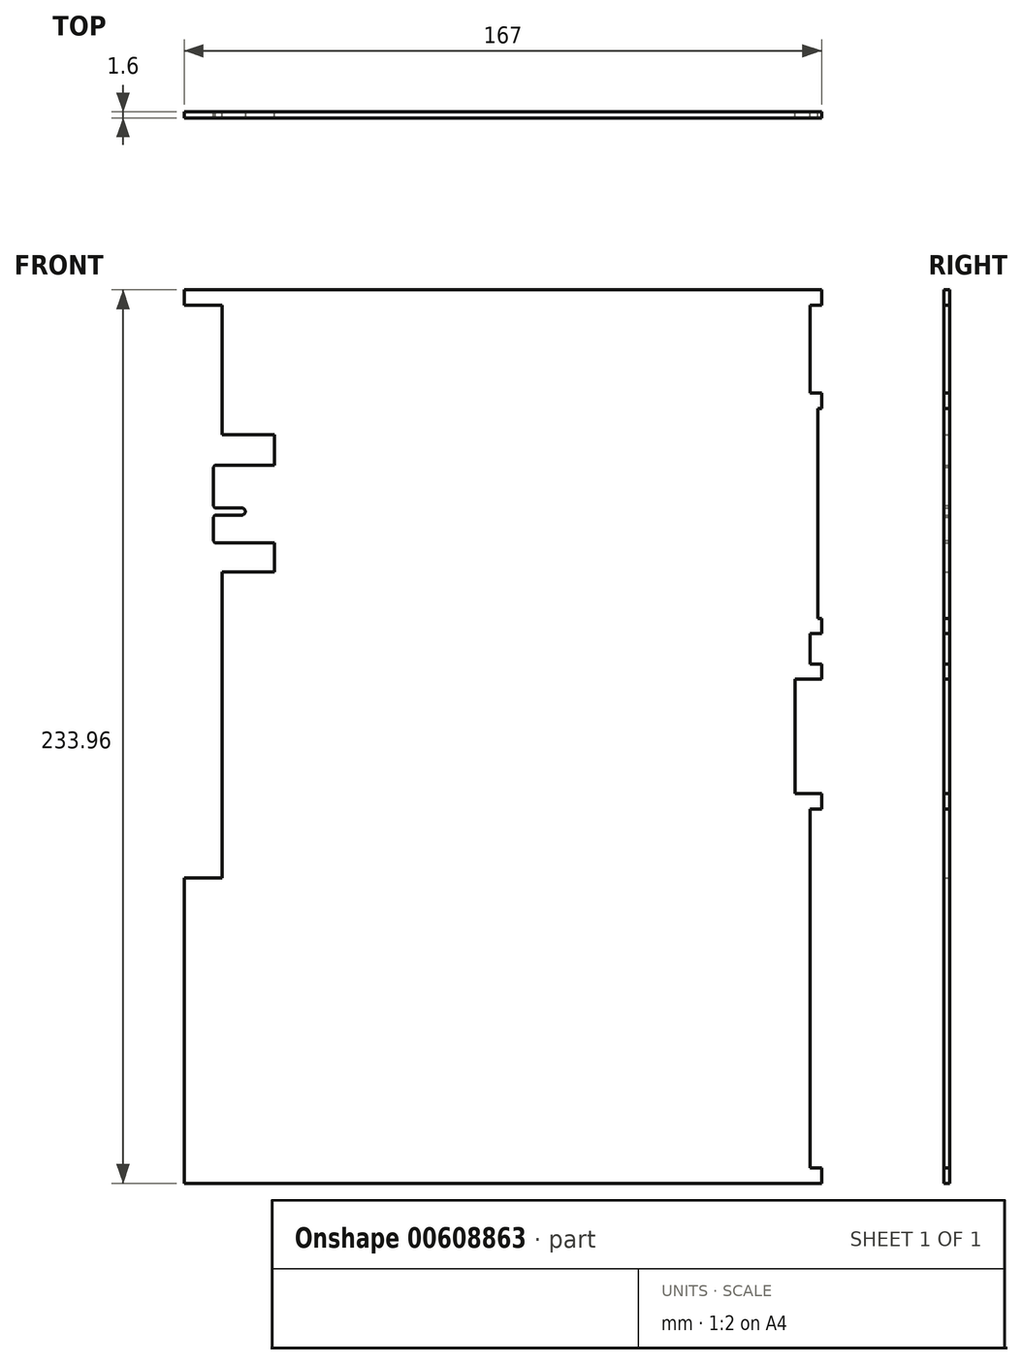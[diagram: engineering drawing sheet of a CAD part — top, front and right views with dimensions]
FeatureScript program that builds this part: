
annotation { "Feature Type Name" : "Feature", "Feature Type Description" : "" }
export const myFeature = defineFeature(function(context is Context, id is Id, definition is map)
    precondition{}
    {
        {
            var Q0;
            Q0=qCreatedBy(makeId("Front.planeOp"),FACE);
            var sketch = newSketch(context, id + "F0", { "sketchPlane" : qUnion([Q0])});
            skLineSegment(sketch, "E0.bottom", {"start": v(0, 0) * mm, "end": v(167, 0) * mm});
            skLineSegment(sketch, "E0.top", {"start": v(0, 233.96) * mm, "end": v(167, 233.96) * mm});
            skLineSegment(sketch, "E0.left", {"start": v(0, 0) * mm, "end": v(0, 233.96) * mm});
            skLineSegment(sketch, "E0.right", {"start": v(167, 0) * mm, "end": v(167, 233.96) * mm});
            skLineSegment(sketch, "E1.bottom", {"start": v(0, 229.96) * mm, "end": v(10, 229.96) * mm});
            skLineSegment(sketch, "E1.top", {"start": v(0, 79.96) * mm, "end": v(10, 79.96) * mm});
            skLineSegment(sketch, "E1.left", {"start": v(0, 229.96) * mm, "end": v(0, 79.96) * mm});
            skLineSegment(sketch, "E1.right", {"start": v(10, 229.96) * mm, "end": v(10, 79.96) * mm});
            skLineSegment(sketch, "E2.bottom", {"start": v(-12.96, 196.1) * mm, "end": v(23.6, 196.1) * mm});
            skLineSegment(sketch, "E2.top", {"start": v(-12.96, 160.1) * mm, "end": v(23.6, 160.1) * mm});
            skLineSegment(sketch, "E2.left", {"start": v(-12.96, 196.1) * mm, "end": v(-12.96, 160.1) * mm});
            skLineSegment(sketch, "E2.right", {"start": v(23.6, 196.1) * mm, "end": v(23.6, 160.1) * mm});
            skLineSegment(sketch, "E3.bottom", {"start": v(7.6, 188.07) * mm, "end": v(33.85, 188.07) * mm});
            skLineSegment(sketch, "E3.top", {"start": v(7.6, 167.77) * mm, "end": v(33.85, 167.77) * mm});
            skLineSegment(sketch, "E3.left", {"start": v(7.6, 188.07) * mm, "end": v(7.6, 167.77) * mm});
            skLineSegment(sketch, "E3.right", {"start": v(33.85, 188.07) * mm, "end": v(33.85, 167.77) * mm});
            skLineSegment(sketch, "E4.bottom", {"start": v(4.67, 176.87) * mm, "end": v(16, 176.87) * mm});
            skLineSegment(sketch, "E4.top", {"start": v(4.67, 174.97) * mm, "end": v(16, 174.97) * mm});
            skLineSegment(sketch, "E4.left", {"start": v(4.67, 176.87) * mm, "end": v(4.67, 174.97) * mm});
            skLineSegment(sketch, "E4.right", {"start": v(16, 176.87) * mm, "end": v(16, 174.97) * mm});
            skLineSegment(sketch, "E5.bottom", {"start": v(167, 4) * mm, "end": v(164, 4) * mm});
            skLineSegment(sketch, "E5.top", {"start": v(167, 98) * mm, "end": v(164, 98) * mm});
            skLineSegment(sketch, "E5.left", {"start": v(167, 4) * mm, "end": v(167, 98) * mm});
            skLineSegment(sketch, "E5.right", {"start": v(164, 4) * mm, "end": v(164, 98) * mm});
            skLineSegment(sketch, "E6.bottom", {"start": v(167, 102) * mm, "end": v(160, 102) * mm});
            skLineSegment(sketch, "E6.top", {"start": v(167, 132) * mm, "end": v(160, 132) * mm});
            skLineSegment(sketch, "E6.left", {"start": v(167, 102) * mm, "end": v(167, 132) * mm});
            skLineSegment(sketch, "E6.right", {"start": v(160, 102) * mm, "end": v(160, 132) * mm});
            skLineSegment(sketch, "E7.bottom", {"start": v(167, 136) * mm, "end": v(164, 136) * mm});
            skLineSegment(sketch, "E7.top", {"start": v(167, 144) * mm, "end": v(164, 144) * mm});
            skLineSegment(sketch, "E7.left", {"start": v(167, 136) * mm, "end": v(167, 144) * mm});
            skLineSegment(sketch, "E7.right", {"start": v(164, 136) * mm, "end": v(164, 144) * mm});
            skLineSegment(sketch, "E8.bottom", {"start": v(167, 147.96) * mm, "end": v(166, 147.96) * mm});
            skLineSegment(sketch, "E8.top", {"start": v(167, 202.96) * mm, "end": v(166, 202.96) * mm});
            skLineSegment(sketch, "E8.left", {"start": v(167, 147.96) * mm, "end": v(167, 202.96) * mm});
            skLineSegment(sketch, "E8.right", {"start": v(166, 147.96) * mm, "end": v(166, 202.96) * mm});
            skLineSegment(sketch, "E9.bottom", {"start": v(167, 229.96) * mm, "end": v(164, 229.96) * mm});
            skLineSegment(sketch, "E9.top", {"start": v(167, 206.96) * mm, "end": v(164, 206.96) * mm});
            skLineSegment(sketch, "E9.left", {"start": v(167, 229.96) * mm, "end": v(167, 206.96) * mm});
            skLineSegment(sketch, "E9.right", {"start": v(164, 229.96) * mm, "end": v(164, 206.96) * mm});
            skSolve(sketch);
        }
        {
            var Q0;
            {var subQ19=sQuery(id+"F0.wireOp",EDGE,"E0.bottom");Q0=makeQuery(id+"F0.imprint","IMPRINT",FACE,{"disambiguationData":[TD([[makeQuery(id+"F0.imprint","IMPRINT",EDGE,{"derivedFrom":subQ19}),1.0]])]});}
            var Q1;
            {var subQ5=sQuery(id+"F0.wireOp",EDGE,"E3.right");Q1=makeQuery(id+"F0.imprint","IMPRINT",FACE,{"disambiguationData":[TD([[makeQuery(id+"F0.imprint","IMPRINT",EDGE,{"derivedFrom":subQ5}),-1.0]])]});}
            var Q2;
            {var subQ5=sQuery(id+"F0.wireOp",EDGE,"E4.right");Q2=makeQuery(id+"F0.imprint","IMPRINT",FACE,{"disambiguationData":[TD([[makeQuery(id+"F0.imprint","IMPRINT",EDGE,{"derivedFrom":subQ5}),1.0]])]});}
            var Q3;
            {var subQ0=sQuery(id+"F0.wireOp",EDGE,"E4.top");var subQ1=sQuery(id+"F0.wireOp",EDGE,"E1.right");var subQ2=makeQuery(id+"F0.imprint","INTERSECT",VERTEX,{"derivedFrom":[subQ1,subQ0]});Q3=makeQuery(id+"F0.imprint","IMPRINT",FACE,{"disambiguationData":[TD([[makeQuery(id+"F0.imprint","IMPRINT",EDGE,{"disambiguationData":[TD([[subQ2,-1.0]])],"derivedFrom":subQ1}),-1.0]])]});}
            var Q4;
            {var subQ0=sQuery(id+"F0.wireOp",EDGE,"E3.bottom");var subQ1=sQuery(id+"F0.wireOp",EDGE,"E1.right");var subQ2=makeQuery(id+"F0.imprint","INTERSECT",VERTEX,{"derivedFrom":[subQ1,subQ0]});Q4=makeQuery(id+"F0.imprint","IMPRINT",FACE,{"disambiguationData":[TD([[makeQuery(id+"F0.imprint","IMPRINT",EDGE,{"disambiguationData":[TD([[subQ2,-1.0]])],"derivedFrom":subQ1}),-1.0]])]});}
            extrude(context, id + "F1", {"entities" : qUnion([Q0, Q1, Q2, Q3, Q4]), "depth" : 1.6 * mm, "offsetDistance" : 25 * mm});
        }
        {
            var Q0;
            Q0=makeQuery(id+"F1.opExtrude","SWEPT_EDGE",EDGE,{"disambiguationData":[OSD([sQuery(id+"F0.wireOp",EDGE,"E3.top"),sQuery(id+"F0.wireOp",EDGE,"E3.left")])]});
            var Q1;
            Q1=makeQuery(id+"F1.opExtrude","SWEPT_EDGE",EDGE,{"disambiguationData":[OSD([sQuery(id+"F0.wireOp",EDGE,"E3.left"),sQuery(id+"F0.wireOp",EDGE,"E4.top")])]});
            var Q2;
            Q2=makeQuery(id+"F1.opExtrude","SWEPT_EDGE",EDGE,{"disambiguationData":[OSD([sQuery(id+"F0.wireOp",EDGE,"E3.left"),sQuery(id+"F0.wireOp",EDGE,"E4.bottom")])]});
            var Q3;
            Q3=makeQuery(id+"F1.opExtrude","SWEPT_EDGE",EDGE,{"disambiguationData":[OSD([sQuery(id+"F0.wireOp",EDGE,"E3.bottom"),sQuery(id+"F0.wireOp",EDGE,"E3.left")])]});
            chamfer(context, id + "F2", {"entities" : qUnion([Q0, Q1, Q2, Q3]), "width" : 0.5 * mm, "tangentPropagation" : true});
        }
        {
            var Q0;
            Q0=makeQuery(id+"F1.opExtrude","SWEPT_EDGE",EDGE,{"disambiguationData":[OSD([sQuery(id+"F0.wireOp",EDGE,"E4.bottom"),sQuery(id+"F0.wireOp",EDGE,"E4.right")])]});
            var Q1;
            Q1=makeQuery(id+"F1.opExtrude","SWEPT_EDGE",EDGE,{"disambiguationData":[OSD([sQuery(id+"F0.wireOp",EDGE,"E4.top"),sQuery(id+"F0.wireOp",EDGE,"E4.right")])]});
            fillet(context, id + "F3", {"entities" : qUnion([Q0, Q1]), "radius" : 0.95 * mm, "tangentPropagation" : true, "allowEdgeOverflow" : false});
        }
    });
